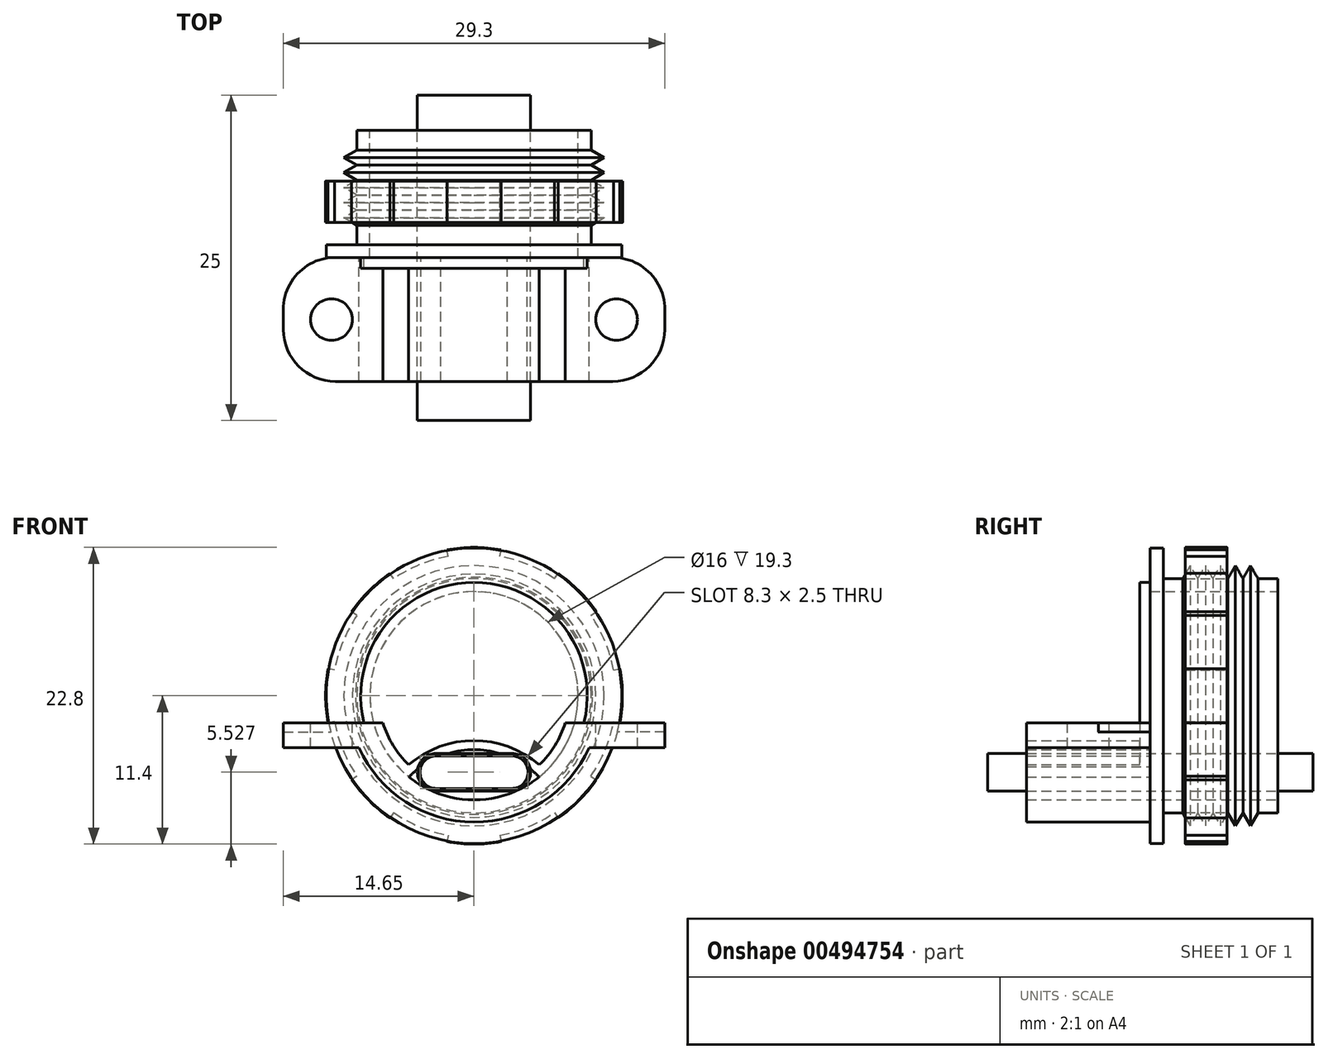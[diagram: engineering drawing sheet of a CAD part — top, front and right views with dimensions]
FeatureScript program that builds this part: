
annotation { "Feature Type Name" : "Feature", "Feature Type Description" : "" }
export const myFeature = defineFeature(function(context is Context, id is Id, definition is map)
    precondition{}
    {
        {
            var Q0;
            Q0=qCreatedBy(makeId("Top.planeOp"),FACE);
            var sketch = newSketch(context, id + "F0", { "sketchPlane" : qUnion([Q0])});
            skLineSegment(sketch, "E0", {"start": v(8, 9.8) * mm, "end": v(8, 0) * mm});
            skLineSegment(sketch, "E1", {"start": v(8, 0) * mm, "end": v(11.35, 0) * mm});
            skLineSegment(sketch, "E2", {"start": v(11.35, 0) * mm, "end": v(11.35, 1) * mm});
            skLineSegment(sketch, "E3", {"start": v(11.35, 1) * mm, "end": v(9, 1) * mm});
            skLineSegment(sketch, "E4", {"start": v(9, 1) * mm, "end": v(9, 2.5) * mm});
            skLineSegment(sketch, "E5", {"start": v(9, 2.5) * mm, "end": v(10, 3.08) * mm});
            skLineSegment(sketch, "E6", {"start": v(10, 3.08) * mm, "end": v(9, 3.65) * mm});
            skLineSegment(sketch, "E7", {"start": v(9, 3.65) * mm, "end": v(10, 4.23) * mm});
            skLineSegment(sketch, "E8", {"start": v(10, 4.23) * mm, "end": v(9, 4.8) * mm});
            skLineSegment(sketch, "E9", {"start": v(9, 4.8) * mm, "end": v(10, 5.39) * mm});
            skLineSegment(sketch, "E10", {"start": v(10, 5.39) * mm, "end": v(9, 5.96) * mm});
            skLineSegment(sketch, "E11", {"start": v(9, 5.96) * mm, "end": v(10, 6.54) * mm});
            skLineSegment(sketch, "E12", {"start": v(10, 6.54) * mm, "end": v(9, 7.12) * mm});
            skLineSegment(sketch, "E13", {"start": v(9, 9.8) * mm, "end": v(8, 9.8) * mm});
            skLineSegment(sketch, "E14", {"start": v(9, 7.12) * mm, "end": v(10, 7.7) * mm});
            skLineSegment(sketch, "E15", {"start": v(10, 7.7) * mm, "end": v(9, 8.27) * mm});
            skLineSegment(sketch, "E16", {"start": v(9, 8.27) * mm, "end": v(9, 9.8) * mm});
            skLineSegment(sketch, "E17", {"start": v(0, 25) * mm, "end": v(0, -25) * mm, "construction": true});
            skPoint(sketch, "E18", {"position": v(0, 0) * mm});
            skSolve(sketch);
        }
        {
            var Q0;
            Q0 = qSketchRegion(id + "F0", true);
            var Q1;
            Q1=sQuery(id+"F0.wireOp",EDGE,"E17");
            revolve(context, id + "F1", {"entities" : qUnion([Q0]), "axis" : qUnion([Q1]), "revolveType" : RevolveType.FULL});
        }
        {
            var Q0;
            Q0=makeQuery(id+"F1.opRevolve","SWEPT_FACE",FACE,{"disambiguationData":[OSD([sQuery(id+"F0.wireOp",EDGE,"E1")])]});
            var sketch = newSketch(context, id + "F2", { "sketchPlane" : qUnion([Q0])});
            skArc(sketch, "E19.0", {"start": v(-7.5, -2.78) * mm, "mid": v(0, -8) * mm, "end": v(7.5, -2.78) * mm});
            skLineSegment(sketch, "E20", {"start": v(-7.5, -2.78) * mm, "end": v(7.5, -2.78) * mm, "construction": true});
            skArc(sketch, "E21.0", {"start": v(-8.84, -3.98) * mm, "mid": v(0, -9.7) * mm, "end": v(8.84, -3.98) * mm});
            skLineSegment(sketch, "E22", {"start": v(-7.5, -2.78) * mm, "end": v(-14.65, -2.78) * mm});
            skLineSegment(sketch, "E23", {"start": v(-14.65, -2.78) * mm, "end": v(-14.65, -3.98) * mm});
            skLineSegment(sketch, "E24", {"start": v(-14.65, -3.98) * mm, "end": v(-8.84, -3.98) * mm});
            skLineSegment(sketch, "E25.MirrorCS", {"start": v(14.65, -3.98) * mm, "end": v(8.84, -3.98) * mm});
            skLineSegment(sketch, "E26.MirrorCS", {"start": v(7.5, -2.78) * mm, "end": v(14.65, -2.78) * mm});
            skLineSegment(sketch, "E27.MirrorCS", {"start": v(14.65, -2.78) * mm, "end": v(14.65, -3.98) * mm});
            skSolve(sketch);
        }
        {
            var Q0;
            Q0 = qSketchRegion(id + "F2", true);
            extrude(context, id + "F3", {"entities" : qUnion([Q0]), "operationType" : NewBodyOperationType.ADD, "depth" : 9.5 * mm});
        }
        {
            var Q0;
            Q0=makeQuery(id+"F3.opExtrude","CAP_EDGE",EDGE,{"disambiguationData":[OSD([sQuery(id+"F2.wireOp",EDGE,"E27.MirrorCS")])],"isStart":true});
            var Q1;
            Q1=makeQuery(id+"F3.opExtrude","CAP_EDGE",EDGE,{"disambiguationData":[OSD([sQuery(id+"F2.wireOp",EDGE,"E27.MirrorCS")])],"isStart":false});
            var Q2;
            Q2=makeQuery(id+"F3.opExtrude","CAP_EDGE",EDGE,{"disambiguationData":[OSD([sQuery(id+"F2.wireOp",EDGE,"E23")])],"isStart":true});
            var Q3;
            Q3=makeQuery(id+"F3.opExtrude","CAP_EDGE",EDGE,{"disambiguationData":[OSD([sQuery(id+"F2.wireOp",EDGE,"E23")])],"isStart":false});
            fillet(context, id + "F4", {"entities" : qUnion([Q0, Q1, Q2, Q3]), "radius" : 4 * mm, "tangentPropagation" : true, "allowEdgeOverflow" : false});
        }
        {
            var Q0;
            Q0=makeQuery(id+"F3.opExtrude","SWEPT_FACE",FACE,{"disambiguationData":[OSD([sQuery(id+"F2.wireOp",EDGE,"E26.MirrorCS")])]});
            var sketch = newSketch(context, id + "F5", { "sketchPlane" : qUnion([Q0])});
            skCircle(sketch, "E28", {"center": v(10.95, -4.75) * mm, "radius": 1.6 * mm});
            skCircle(sketch, "E29.MirrorC", {"center": v(-10.95, -4.75) * mm, "radius": 1.6 * mm});
            skSolve(sketch);
        }
        {
            var Q0;
            Q0 = qSketchRegion(id + "F5", true);
            var Q1;
            Q1=makeQuery(id+"F3.opExtrude","SWEPT_FACE",FACE,{"disambiguationData":[OSD([sQuery(id+"F2.wireOp",EDGE,"E25.MirrorCS")])]});
            extrude(context, id + "F6", {"entities" : qUnion([Q0]), "operationType" : NewBodyOperationType.REMOVE, "endBound" : BoundingType.UP_TO_SURFACE, "oppositeDirection" : true, "endBoundEntityFace" : qUnion([Q1]), "depth" : 25 * mm});
        }
        {
            var Q0;
            Q0=makeQuery(id+"F3.boolean.opBoolean","SPLIT",FACE,{"disambiguationData":[TD([makeQuery(id+"F1.opRevolve","SWEPT_FACE",FACE,{"disambiguationData":[OSD([sQuery(id+"F0.wireOp",EDGE,"E0")])]})])],"derivedFrom":makeQuery(id+"F1.opRevolve","SWEPT_FACE",FACE,{"disambiguationData":[OSD([sQuery(id+"F0.wireOp",EDGE,"E1")])]})});
            var sketch = newSketch(context, id + "F7", { "sketchPlane" : qUnion([Q0])});
            skArc(sketch, "E30.0", {"start": v(7.5, -2.78) * mm, "mid": v(6.49, -4.68) * mm, "end": v(5, -6.24) * mm});
            skLineSegment(sketch, "E31", {"start": v(-5, -6.24) * mm, "end": v(5, -6.24) * mm, "construction": true});
            skArc(sketch, "E32", {"start": v(5, -6.24) * mm, "mid": v(0, -4.14) * mm, "end": v(-5, -6.24) * mm});
            skArc(sketch, "E33.trimOffspring", {"start": v(-5, -6.24) * mm, "mid": v(-6.49, -4.68) * mm, "end": v(-7.5, -2.78) * mm});
            skLineSegment(sketch, "E34", {"start": v(7.5, -2.78) * mm, "end": v(14.65, -2.78) * mm});
            skLineSegment(sketch, "E35", {"start": v(-7.5, -2.78) * mm, "end": v(-14.65, -2.78) * mm});
            skLineSegment(sketch, "E36.0", {"start": v(-7, -2.08) * mm, "end": v(-14.65, -2.08) * mm});
            skLineSegment(sketch, "E36.1", {"start": v(7, -2.08) * mm, "end": v(14.65, -2.08) * mm});
            skArc(sketch, "E36.2", {"start": v(7, -2.08) * mm, "mid": v(6.22, -3.82) * mm, "end": v(5.02, -5.3) * mm});
            skArc(sketch, "E36.3", {"start": v(5.02, -5.3) * mm, "mid": v(0, -3.44) * mm, "end": v(-5.02, -5.3) * mm});
            skArc(sketch, "E36.4", {"start": v(-5.02, -5.3) * mm, "mid": v(-6.22, -3.82) * mm, "end": v(-7, -2.08) * mm});
            skLineSegment(sketch, "E37", {"start": v(-14.65, -2.78) * mm, "end": v(-14.65, -2.08) * mm});
            skLineSegment(sketch, "E38", {"start": v(14.65, -2.78) * mm, "end": v(14.65, -2.08) * mm});
            skSolve(sketch);
        }
        {
            var Q0;
            Q0 = qSketchRegion(id + "F7", true);
            extrude(context, id + "F8", {"entities" : qUnion([Q0]), "depth" : 9.5 * mm});
        }
        {
            var Q0;
            Q0=makeQuery(id+"F8.opExtrude","CAP_FACE",FACE,{"disambiguationData":[OSD([sQuery(id+"F7.wireOp",EDGE,"E30.0"),sQuery(id+"F7.wireOp",EDGE,"E32"),sQuery(id+"F7.wireOp",EDGE,"E33.trimOffspring"),sQuery(id+"F7.wireOp",EDGE,"E34"),sQuery(id+"F7.wireOp",EDGE,"E35"),sQuery(id+"F7.wireOp",EDGE,"E36.0"),sQuery(id+"F7.wireOp",EDGE,"E36.1"),sQuery(id+"F7.wireOp",EDGE,"E36.2"),sQuery(id+"F7.wireOp",EDGE,"E36.3"),sQuery(id+"F7.wireOp",EDGE,"E36.4"),sQuery(id+"F7.wireOp",EDGE,"E37"),sQuery(id+"F7.wireOp",EDGE,"E38")])],"isStart":true});
            var sketch = newSketch(context, id + "F9", { "sketchPlane" : qUnion([Q0])});
            skArc(sketch, "E39.0", {"start": v(7.72, -2.08) * mm, "mid": v(0, 8) * mm, "end": v(-7.72, -2.08) * mm, "construction": true});
            skArc(sketch, "E40.0", {"start": v(-7, -2.08) * mm, "mid": v(-6.22, -3.82) * mm, "end": v(-5.02, -5.3) * mm, "construction": true});
            skArc(sketch, "E40.1", {"start": v(-5.02, -5.3) * mm, "mid": v(0, -3.44) * mm, "end": v(5.02, -5.3) * mm, "construction": true});
            skArc(sketch, "E40.2", {"start": v(5.02, -5.3) * mm, "mid": v(6.22, -3.82) * mm, "end": v(7, -2.08) * mm, "construction": true});
            skLineSegment(sketch, "E40.3", {"start": v(7, -2.08) * mm, "end": v(7.72, -2.08) * mm, "construction": true});
            skLineSegment(sketch, "E40.4", {"start": v(-7, -2.08) * mm, "end": v(-7.72, -2.08) * mm, "construction": true});
            skPoint(sketch, "E41.orphan", {"position": v(-14.65, -2.08) * mm});
            skPoint(sketch, "E42.orphan", {"position": v(14.65, -2.08) * mm});
            skLineSegment(sketch, "E43.0", {"start": v(7.5, -2.78) * mm, "end": v(8.24, -2.78) * mm});
            skLineSegment(sketch, "E43.1", {"start": v(-7.5, -2.78) * mm, "end": v(-8.24, -2.78) * mm});
            skArc(sketch, "E43.2", {"start": v(-7.5, -2.78) * mm, "mid": v(-6.49, -4.68) * mm, "end": v(-5, -6.24) * mm});
            skArc(sketch, "E43.3", {"start": v(8.24, -2.78) * mm, "mid": v(0, 8.7) * mm, "end": v(-8.24, -2.78) * mm});
            skArc(sketch, "E43.4", {"start": v(-5, -6.24) * mm, "mid": v(0, -4.14) * mm, "end": v(5, -6.24) * mm});
            skArc(sketch, "E43.5", {"start": v(5, -6.24) * mm, "mid": v(6.49, -4.68) * mm, "end": v(7.5, -2.78) * mm});
            skSolve(sketch);
        }
        {
            var Q0;
            Q0 = qSketchRegion(id + "F9", true);
            extrude(context, id + "F10", {"entities" : qUnion([Q0]), "operationType" : NewBodyOperationType.ADD, "oppositeDirection" : true, "depth" : 0.8 * mm});
        }
        {
            var Q0;
            Q0=makeQuery(id+"F8.opExtrude","CAP_EDGE",EDGE,{"disambiguationData":[OSD([sQuery(id+"F7.wireOp",EDGE,"E38")])],"isStart":false});
            var Q1;
            Q1=makeQuery(id+"F8.opExtrude","CAP_EDGE",EDGE,{"disambiguationData":[OSD([sQuery(id+"F7.wireOp",EDGE,"E38")])],"isStart":true});
            var Q2;
            Q2=makeQuery(id+"F8.opExtrude","CAP_EDGE",EDGE,{"disambiguationData":[OSD([sQuery(id+"F7.wireOp",EDGE,"E37")])],"isStart":true});
            var Q3;
            Q3=makeQuery(id+"F8.opExtrude","CAP_EDGE",EDGE,{"disambiguationData":[OSD([sQuery(id+"F7.wireOp",EDGE,"E37")])],"isStart":false});
            fillet(context, id + "F11", {"entities" : qUnion([Q0, Q1, Q2, Q3]), "radius" : 4 * mm, "tangentPropagation" : true, "allowEdgeOverflow" : false});
        }
        {
            var Q0;
            Q0=makeQuery(id+"F8.opExtrude","SWEPT_FACE",FACE,{"disambiguationData":[OSD([sQuery(id+"F7.wireOp",EDGE,"E36.1")])]});
            var sketch = newSketch(context, id + "F12", { "sketchPlane" : qUnion([Q0])});
            skCircle(sketch, "E44.0", {"center": v(10.95, -4.75) * mm, "radius": 1.6 * mm});
            skCircle(sketch, "E44.1", {"center": v(-10.95, -4.75) * mm, "radius": 1.6 * mm});
            skSolve(sketch);
        }
        {
            var Q0;
            Q0 = qSketchRegion(id + "F12", true);
            var Q1;
            Q1=makeQuery(id+"F8.opExtrude","SWEPT_FACE",FACE,{"disambiguationData":[OSD([sQuery(id+"F7.wireOp",EDGE,"E34")])]});
            extrude(context, id + "F13", {"entities" : qUnion([Q0]), "operationType" : NewBodyOperationType.REMOVE, "endBound" : BoundingType.UP_TO_SURFACE, "oppositeDirection" : true, "endBoundEntityFace" : qUnion([Q1]), "depth" : 25 * mm});
        }
        {
            var Q0;
            Q0=qCreatedBy(makeId("Top.planeOp"),FACE);
            var sketch = newSketch(context, id + "F14", { "sketchPlane" : qUnion([Q0])});
            skLineSegment(sketch, "E45.0", {"start": v(10, 5.39) * mm, "end": v(9.11, 5.9) * mm});
            skLineSegment(sketch, "E45.2", {"start": v(9, 4.8) * mm, "end": v(10, 5.39) * mm});
            skLineSegment(sketch, "E45.3", {"start": v(10, 4.23) * mm, "end": v(9, 4.8) * mm});
            skLineSegment(sketch, "E45.4", {"start": v(9, 3.65) * mm, "end": v(10, 4.23) * mm});
            skLineSegment(sketch, "E45.5", {"start": v(10, 3.08) * mm, "end": v(9, 3.65) * mm});
            skLineSegment(sketch, "E45.6", {"start": v(9.35, 2.7) * mm, "end": v(10, 3.08) * mm});
            skLineSegment(sketch, "E45.7", {"start": v(9, 1) * mm, "end": v(9, 2.5) * mm, "construction": true});
            skLineSegment(sketch, "E46", {"start": v(11.4, 5.9) * mm, "end": v(11.4, 2.7) * mm});
            skLineSegment(sketch, "E47", {"start": v(11.4, 5.9) * mm, "end": v(9.11, 5.9) * mm});
            skLineSegment(sketch, "E48", {"start": v(11.4, 2.7) * mm, "end": v(9.35, 2.7) * mm});
            skPoint(sketch, "E49.orphan", {"position": v(9, 2.5) * mm});
            skPoint(sketch, "E45.1.start.orphan", {"position": v(9, 5.96) * mm});
            skPoint(sketch, "E45.9.start.orphan", {"position": v(9, 7.12) * mm});
            skPoint(sketch, "E45.10.end.orphan", {"position": v(9, 8.27) * mm});
            skPoint(sketch, "E45.10.start.orphan", {"position": v(10, 7.7) * mm});
            skPoint(sketch, "E45.11.end.orphan", {"position": v(9, 9.8) * mm});
            skLineSegment(sketch, "E50.0", {"start": v(0, 25) * mm, "end": v(0, -25) * mm, "construction": true});
            skSolve(sketch);
        }
        {
            var Q0;
            Q0 = qSketchRegion(id + "F14", true);
            var Q1;
            Q1=sQuery(id+"F14.wireOp",EDGE,"E50.0");
            revolve(context, id + "F15", {"entities" : qUnion([Q0]), "axis" : qUnion([Q1]), "revolveType" : RevolveType.FULL});
        }
        {
            var Q0;
            Q0=makeQuery(id+"F15.opRevolve","SWEPT_FACE",FACE,{"disambiguationData":[OSD([sQuery(id+"F14.wireOp",EDGE,"E47")])]});
            var sketch = newSketch(context, id + "F16", { "sketchPlane" : qUnion([Q0])});
            skArc(sketch, "E51.0", {"start": v(-2.08, 11.2) * mm, "mid": v(-4.36, 10.53) * mm, "end": v(-6.45, 9.4) * mm});
            skArc(sketch, "E52.0", {"start": v(-2, 10.72) * mm, "mid": v(-4.17, 10.07) * mm, "end": v(-6.17, 8.99) * mm});
            skLineSegment(sketch, "E53", {"start": v(0, 0) * mm, "end": v(0, 10.9) * mm, "construction": true});
            skLineSegment(sketch, "E54", {"start": v(0, 0) * mm, "end": v(-2, 10.72) * mm, "construction": true});
            skLineSegment(sketch, "E55.MirrorCS", {"start": v(0, 0) * mm, "end": v(2, 10.72) * mm, "construction": true});
            skLineSegment(sketch, "E56", {"start": v(-2, 10.72) * mm, "end": v(-2.08, 11.2) * mm});
            skLineSegment(sketch, "E57", {"start": v(2, 10.72) * mm, "end": v(2.08, 11.2) * mm});
            skLineSegment(sketch, "E58.1.0", {"start": v(-8.99, 6.17) * mm, "end": v(-9.4, 6.45) * mm});
            skLineSegment(sketch, "E58.1.1", {"start": v(-6.17, 8.99) * mm, "end": v(-6.45, 9.4) * mm});
            skLineSegment(sketch, "E58.2.0", {"start": v(-10.72, -2) * mm, "end": v(-11.2, -2.08) * mm});
            skLineSegment(sketch, "E58.2.1", {"start": v(-10.72, 2) * mm, "end": v(-11.2, 2.08) * mm});
            skLineSegment(sketch, "E58.3.0", {"start": v(-6.17, -8.99) * mm, "end": v(-6.45, -9.4) * mm});
            skLineSegment(sketch, "E58.3.1", {"start": v(-8.99, -6.17) * mm, "end": v(-9.4, -6.45) * mm});
            skLineSegment(sketch, "E58.4.0", {"start": v(2, -10.72) * mm, "end": v(2.08, -11.2) * mm});
            skLineSegment(sketch, "E58.4.1", {"start": v(-2, -10.72) * mm, "end": v(-2.08, -11.2) * mm});
            skLineSegment(sketch, "E58.5.0", {"start": v(8.99, -6.17) * mm, "end": v(9.4, -6.45) * mm});
            skLineSegment(sketch, "E58.5.1", {"start": v(6.17, -8.99) * mm, "end": v(6.45, -9.4) * mm});
            skLineSegment(sketch, "E58.6.0", {"start": v(10.72, 2) * mm, "end": v(11.2, 2.08) * mm});
            skLineSegment(sketch, "E58.6.1", {"start": v(10.72, -2) * mm, "end": v(11.2, -2.08) * mm});
            skLineSegment(sketch, "E58.7.0", {"start": v(6.17, 8.99) * mm, "end": v(6.45, 9.4) * mm});
            skLineSegment(sketch, "E58.7.1", {"start": v(8.99, 6.17) * mm, "end": v(9.4, 6.45) * mm});
            skArc(sketch, "E59.trimOffspring", {"start": v(6.45, 9.4) * mm, "mid": v(4.36, 10.53) * mm, "end": v(2.08, 11.2) * mm});
            skArc(sketch, "E60.trimOffspring", {"start": v(6.17, 8.99) * mm, "mid": v(4.17, 10.07) * mm, "end": v(2, 10.72) * mm});
            skArc(sketch, "E61.trimOffspring", {"start": v(11.2, 2.08) * mm, "mid": v(10.53, 4.36) * mm, "end": v(9.4, 6.45) * mm});
            skArc(sketch, "E62.trimOffspring", {"start": v(10.72, 2) * mm, "mid": v(10.07, 4.17) * mm, "end": v(8.99, 6.17) * mm});
            skArc(sketch, "E63.trimOffspring", {"start": v(-9.4, 6.45) * mm, "mid": v(-10.53, 4.36) * mm, "end": v(-11.2, 2.08) * mm});
            skArc(sketch, "E64.trimOffspring", {"start": v(-8.99, 6.17) * mm, "mid": v(-10.07, 4.17) * mm, "end": v(-10.72, 2) * mm});
            skArc(sketch, "E65.trimOffspring", {"start": v(8.99, -6.17) * mm, "mid": v(10.07, -4.17) * mm, "end": v(10.72, -2) * mm});
            skArc(sketch, "E66.trimOffspring", {"start": v(9.4, -6.45) * mm, "mid": v(10.53, -4.36) * mm, "end": v(11.2, -2.08) * mm});
            skArc(sketch, "E67.trimOffspring", {"start": v(-10.72, -2) * mm, "mid": v(-10.07, -4.17) * mm, "end": v(-8.99, -6.17) * mm});
            skArc(sketch, "E68.trimOffspring", {"start": v(-11.2, -2.08) * mm, "mid": v(-10.53, -4.36) * mm, "end": v(-9.4, -6.45) * mm});
            skArc(sketch, "E69.trimOffspring", {"start": v(-6.17, -8.99) * mm, "mid": v(-4.17, -10.07) * mm, "end": v(-2, -10.72) * mm});
            skArc(sketch, "E70.trimOffspring", {"start": v(-6.45, -9.4) * mm, "mid": v(-4.36, -10.53) * mm, "end": v(-2.08, -11.2) * mm});
            skArc(sketch, "E71.trimOffspring", {"start": v(2, -10.72) * mm, "mid": v(4.17, -10.07) * mm, "end": v(6.17, -8.99) * mm});
            skArc(sketch, "E72.trimOffspring", {"start": v(2.08, -11.2) * mm, "mid": v(4.36, -10.53) * mm, "end": v(6.45, -9.4) * mm});
            skSolve(sketch);
        }
        {
            var Q0;
            Q0 = qSketchRegion(id + "F16", true);
            var Q1;
            Q1=makeQuery(id+"F15.opRevolve","SWEPT_FACE",FACE,{"disambiguationData":[OSD([sQuery(id+"F14.wireOp",EDGE,"E48")])]});
            extrude(context, id + "F17", {"entities" : qUnion([Q0]), "operationType" : NewBodyOperationType.REMOVE, "endBound" : BoundingType.UP_TO_SURFACE, "oppositeDirection" : true, "endBoundEntityFace" : qUnion([Q1]), "depth" : 25 * mm});
        }
        {
            var Q0;
            Q0=qCreatedBy(makeId("Front.planeOp"),FACE);
            var sketch = newSketch(context, id + "F18", { "sketchPlane" : qUnion([Q0])});
            skArc(sketch, "E73.0", {"start": v(5, -6.24) * mm, "mid": v(0, -4.14) * mm, "end": v(-5, -6.24) * mm, "construction": true});
            skArc(sketch, "E73.1", {"start": v(7.5, -2.78) * mm, "mid": v(0, -8) * mm, "end": v(-7.5, -2.78) * mm, "construction": true});
            skCircle(sketch, "E74", {"center": v(-2.9, -5.87) * mm, "radius": 1.45 * mm, "construction": true});
            skCircle(sketch, "E75", {"center": v(2.9, -5.87) * mm, "radius": 1.45 * mm, "construction": true});
            skCircle(sketch, "E76", {"center": v(0, -5.87) * mm, "radius": 1.45 * mm, "construction": true});
            skCircle(sketch, "E77", {"center": v(2.9, -5.87) * mm, "radius": 1.02 * mm, "construction": true});
            skCircle(sketch, "E78", {"center": v(0, -5.87) * mm, "radius": 1.02 * mm, "construction": true});
            skCircle(sketch, "E79", {"center": v(-2.9, -5.87) * mm, "radius": 1.02 * mm, "construction": true});
            skLineSegment(sketch, "E80", {"start": v(0, -4.14) * mm, "end": v(0, -8) * mm, "construction": true});
            skLineSegment(sketch, "E81", {"start": v(-2.9, -4.42) * mm, "end": v(2.9, -4.42) * mm});
            skLineSegment(sketch, "E82", {"start": v(-2.9, -7.32) * mm, "end": v(2.9, -7.32) * mm});
            skArc(sketch, "E83", {"start": v(2.9, -7.32) * mm, "mid": v(4.35, -5.87) * mm, "end": v(2.9, -4.42) * mm});
            skArc(sketch, "E84", {"start": v(-2.9, -4.42) * mm, "mid": v(-4.35, -5.87) * mm, "end": v(-2.9, -7.32) * mm});
            skSolve(sketch);
        }
        {
            var Q0;
            Q0 = qSketchRegion(id + "F18", true);
            extrude(context, id + "F19", {"entities" : qUnion([Q0]), "endBound" : BoundingType.SYMMETRIC, "depth" : 25 * mm});
        }
        {
            var Q0;
            Q0=makeQuery(id+"F19.opExtrude","CAP_FACE",FACE,{"disambiguationData":[OSD([sQuery(id+"F18.wireOp",EDGE,"E81"),sQuery(id+"F18.wireOp",EDGE,"E82"),sQuery(id+"F18.wireOp",EDGE,"E83"),sQuery(id+"F18.wireOp",EDGE,"E84")])],"isStart":true});
            var sketch = newSketch(context, id + "F20", { "sketchPlane" : qUnion([Q0])});
            skLineSegment(sketch, "E85.0", {"start": v(2.9, -4.62) * mm, "end": v(-2.9, -4.62) * mm});
            skArc(sketch, "E85.1", {"start": v(2.9, -4.62) * mm, "mid": v(4.15, -5.87) * mm, "end": v(2.9, -7.12) * mm});
            skLineSegment(sketch, "E85.2", {"start": v(2.9, -7.12) * mm, "end": v(-2.9, -7.12) * mm});
            skArc(sketch, "E85.3", {"start": v(-2.9, -7.12) * mm, "mid": v(-4.15, -5.87) * mm, "end": v(-2.9, -4.62) * mm});
            skSolve(sketch);
        }
        {
            var Q0;
            Q0 = qSketchRegion(id + "F20", true);
            var Q1;
            Q1=makeQuery(id+"F19.opExtrude","CAP_FACE",FACE,{"disambiguationData":[OSD([sQuery(id+"F18.wireOp",EDGE,"E81"),sQuery(id+"F18.wireOp",EDGE,"E82"),sQuery(id+"F18.wireOp",EDGE,"E83"),sQuery(id+"F18.wireOp",EDGE,"E84")])],"isStart":false});
            extrude(context, id + "F21", {"entities" : qUnion([Q0]), "operationType" : NewBodyOperationType.REMOVE, "endBound" : BoundingType.UP_TO_SURFACE, "oppositeDirection" : true, "endBoundEntityFace" : qUnion([Q1]), "depth" : 2.5 * mm});
        }
    });
